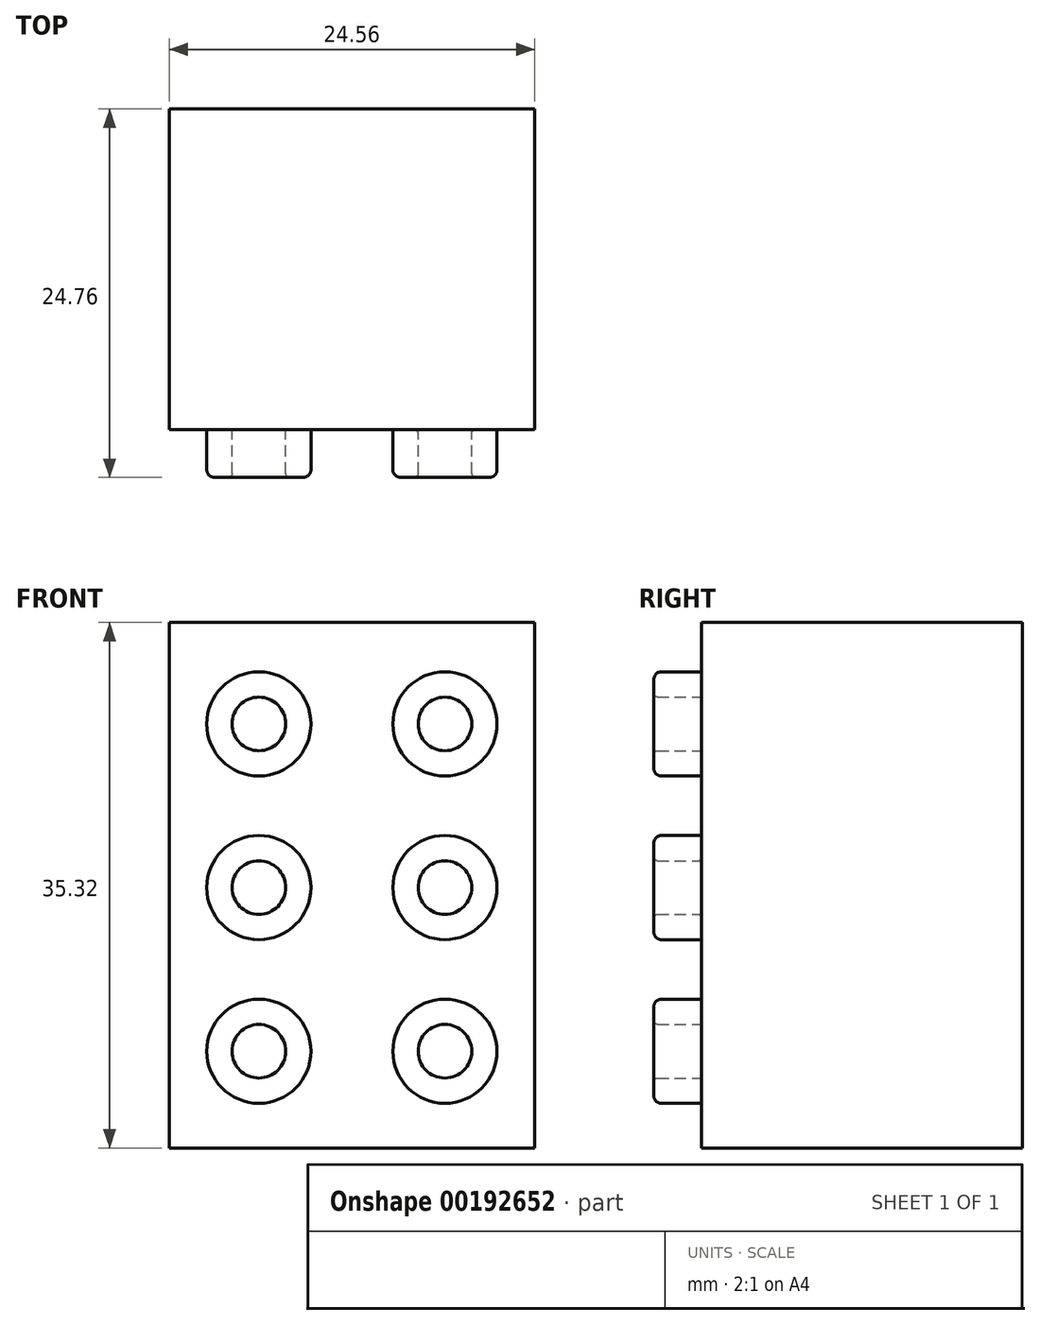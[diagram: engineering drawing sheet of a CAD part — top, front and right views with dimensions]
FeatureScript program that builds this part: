
annotation { "Feature Type Name" : "Feature", "Feature Type Description" : "" }
export const myFeature = defineFeature(function(context is Context, id is Id, definition is map)
    precondition{}
    {
        {
            var Q0;
            Q0=qCreatedBy(makeId("Top.planeOp"),FACE);
            var sketch = newSketch(context, id + "F4", { "sketchPlane" : qUnion([Q0])});
            skLineSegment(sketch, "E0.bottom", {"start": v(-12.28, 10.78) * mm, "end": v(12.28, 10.78) * mm});
            skLineSegment(sketch, "E0.top", {"start": v(-12.28, -10.78) * mm, "end": v(12.28, -10.78) * mm});
            skLineSegment(sketch, "E0.left", {"start": v(-12.28, 10.78) * mm, "end": v(-12.28, -10.78) * mm});
            skLineSegment(sketch, "E0.right", {"start": v(12.28, 10.78) * mm, "end": v(12.28, -10.78) * mm});
            skPoint(sketch, "E0.middle", {"position": v(0, 0) * mm});
            skSolve(sketch);
        }
        {
            var Q0;
            Q0 = qSketchRegion(id + "F4", true);
            extrude(context, id + "F0", {"entities" : qUnion([Q0]), "depth" : 35.32 * mm});
        }
        {
            var Q0;
            Q0=makeQuery(id+"F0.opExtrude","SWEPT_FACE",FACE,{"disambiguationData":[OSD([sQuery(id+"F4.wireOp",EDGE,"E0.top")])]});
            var sketch = newSketch(context, id + "F5", { "sketchPlane" : qUnion([Q0])});
            skLineSegment(sketch, "E1", {"start": v(-6.25, 28.5) * mm, "end": v(-6.25, 6.5) * mm, "construction": true});
            skLineSegment(sketch, "E2", {"start": v(6.25, 6.5) * mm, "end": v(6.25, 28.5) * mm, "construction": true});
            skCircle(sketch, "E3", {"center": v(-6.25, 28.5) * mm, "radius": 3.5 * mm});
            skCircle(sketch, "E4", {"center": v(6.25, 28.5) * mm, "radius": 3.5 * mm});
            skCircle(sketch, "E5", {"center": v(6.25, 6.5) * mm, "radius": 3.5 * mm});
            skCircle(sketch, "E6", {"center": v(-6.25, 6.5) * mm, "radius": 3.5 * mm});
            skCircle(sketch, "E7", {"center": v(-6.25, 17.5) * mm, "radius": 3.5 * mm});
            skCircle(sketch, "E8", {"center": v(6.25, 17.5) * mm, "radius": 3.5 * mm});
            skCircle(sketch, "E9", {"center": v(-6.25, 28.5) * mm, "radius": 1.8 * mm});
            skCircle(sketch, "E10", {"center": v(6.25, 28.5) * mm, "radius": 1.8 * mm});
            skCircle(sketch, "E11", {"center": v(-6.25, 17.5) * mm, "radius": 1.8 * mm});
            skCircle(sketch, "E12", {"center": v(6.25, 17.5) * mm, "radius": 1.8 * mm});
            skCircle(sketch, "E13", {"center": v(6.25, 6.5) * mm, "radius": 1.8 * mm});
            skCircle(sketch, "E14", {"center": v(-6.25, 6.5) * mm, "radius": 1.8 * mm});
            skSolve(sketch);
        }
        {
            var Q0;
            Q0 = qSketchRegion(id + "F5", true);
            extrude(context, id + "F1", {"entities" : qUnion([Q0]), "depth" : 3.2 * mm});
        }
        {
            var Q0;
            Q0=makeQuery(id+"F1.opExtrude","CAP_EDGE",EDGE,{"disambiguationData":[OSD([sQuery(id+"F5.wireOp",EDGE,"E3")])],"isStart":false});
            var Q1;
            Q1=makeQuery(id+"F1.opExtrude","CAP_EDGE",EDGE,{"disambiguationData":[OSD([sQuery(id+"F5.wireOp",EDGE,"E4")])],"isStart":false});
            var Q2;
            Q2=makeQuery(id+"F1.opExtrude","CAP_EDGE",EDGE,{"disambiguationData":[OSD([sQuery(id+"F5.wireOp",EDGE,"E7")])],"isStart":false});
            var Q3;
            Q3=makeQuery(id+"F1.opExtrude","CAP_EDGE",EDGE,{"disambiguationData":[OSD([sQuery(id+"F5.wireOp",EDGE,"E8")])],"isStart":false});
            var Q4;
            Q4=makeQuery(id+"F1.opExtrude","CAP_EDGE",EDGE,{"disambiguationData":[OSD([sQuery(id+"F5.wireOp",EDGE,"E6")])],"isStart":false});
            var Q5;
            Q5=makeQuery(id+"F1.opExtrude","CAP_EDGE",EDGE,{"disambiguationData":[OSD([sQuery(id+"F5.wireOp",EDGE,"E5")])],"isStart":false});
            fillet(context, id + "F2", {"entities" : qUnion([Q0, Q1, Q2, Q3, Q4, Q5]), "radius" : 0.5 * mm, "tangentPropagation" : true, "allowEdgeOverflow" : false});
        }
        {
            var Q0;
            Q0=makeQuery(id+"F1.opExtrude","CAP_EDGE",EDGE,{"disambiguationData":[OSD([sQuery(id+"F5.wireOp",EDGE,"E9")])],"isStart":false});
            var Q1;
            Q1=makeQuery(id+"F1.opExtrude","CAP_EDGE",EDGE,{"disambiguationData":[OSD([sQuery(id+"F5.wireOp",EDGE,"E10")])],"isStart":false});
            var Q2;
            Q2=makeQuery(id+"F1.opExtrude","CAP_EDGE",EDGE,{"disambiguationData":[OSD([sQuery(id+"F5.wireOp",EDGE,"E11")])],"isStart":false});
            var Q3;
            Q3=makeQuery(id+"F1.opExtrude","SWEPT_FACE",FACE,{"disambiguationData":[OSD([sQuery(id+"F5.wireOp",EDGE,"E12")])]});
            var Q4;
            Q4=makeQuery(id+"F1.opExtrude","CAP_EDGE",EDGE,{"disambiguationData":[OSD([sQuery(id+"F5.wireOp",EDGE,"E12")])],"isStart":false});
            var Q5;
            Q5=makeQuery(id+"F1.opExtrude","CAP_EDGE",EDGE,{"disambiguationData":[OSD([sQuery(id+"F5.wireOp",EDGE,"E14")])],"isStart":false});
            var Q6;
            Q6=makeQuery(id+"F1.opExtrude","CAP_EDGE",EDGE,{"disambiguationData":[OSD([sQuery(id+"F5.wireOp",EDGE,"E13")])],"isStart":false});
            fillet(context, id + "F3", {"entities" : qUnion([Q0, Q1, Q2, Q3, Q4, Q5, Q6]), "radius" : 0.25 * mm, "tangentPropagation" : true, "allowEdgeOverflow" : false});
        }
    });
